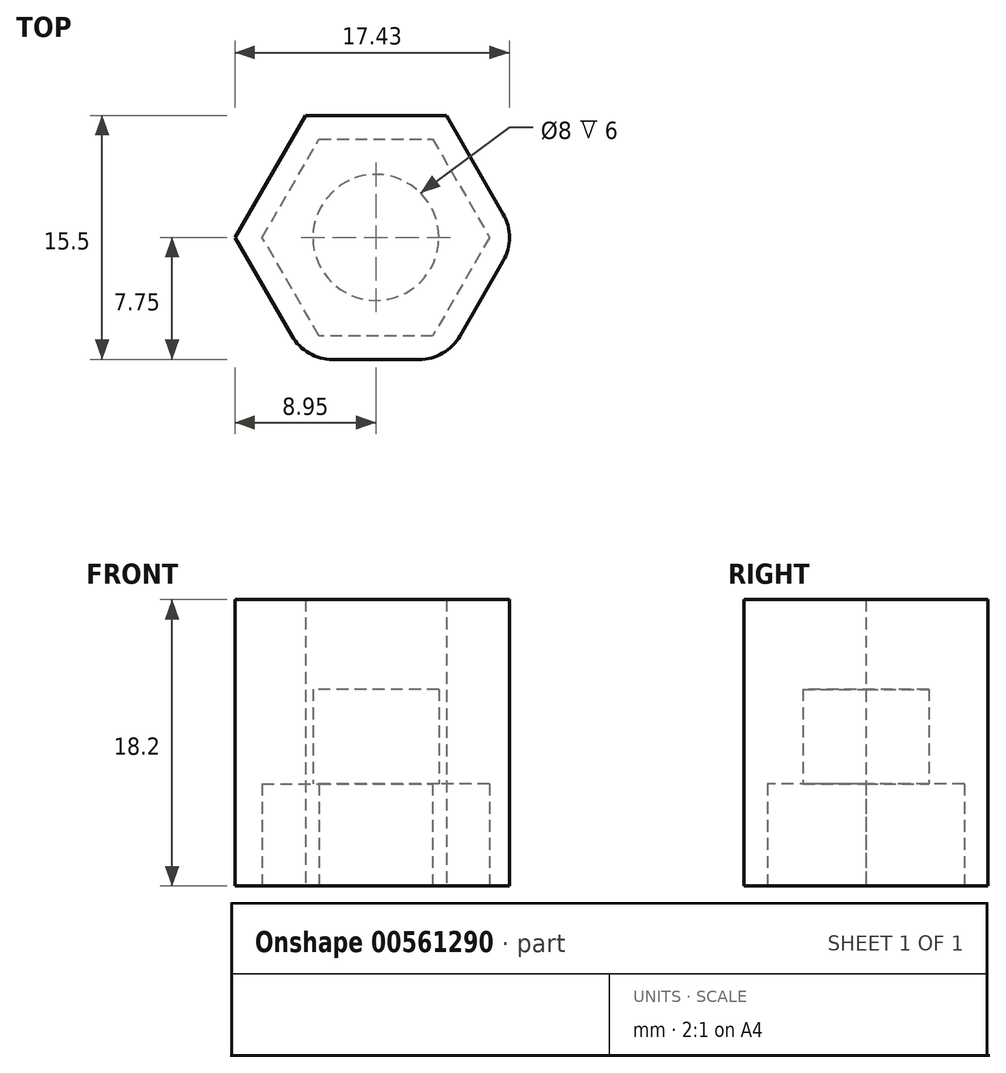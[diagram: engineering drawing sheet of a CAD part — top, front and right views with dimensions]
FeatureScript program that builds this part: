
annotation { "Feature Type Name" : "Feature", "Feature Type Description" : "" }
export const myFeature = defineFeature(function(context is Context, id is Id, definition is map)
    precondition{}
    {
        {
            var Q0;
            Q0=qCreatedBy(makeId("Top.planeOp"),FACE);
            var sketch = newSketch(context, id + "F0", { "sketchPlane" : qUnion([Q0])});
            skCircle(sketch, "E0.cCircle", {"center": v(0, 0) * mm, "radius": 7.75 * mm, "construction": true});
            skLineSegment(sketch, "E0.0", {"start": v(8.95, 0) * mm, "end": v(4.47, -7.75) * mm});
            skLineSegment(sketch, "E0.1", {"start": v(4.47, -7.75) * mm, "end": v(-4.47, -7.75) * mm});
            skLineSegment(sketch, "E0.2", {"start": v(-4.47, -7.75) * mm, "end": v(-8.95, 0) * mm});
            skLineSegment(sketch, "E0.3", {"start": v(-8.95, 0) * mm, "end": v(-4.47, 7.75) * mm});
            skLineSegment(sketch, "E0.4", {"start": v(-4.47, 7.75) * mm, "end": v(4.47, 7.75) * mm});
            skLineSegment(sketch, "E0.5", {"start": v(4.47, 7.75) * mm, "end": v(8.95, 0) * mm});
            skPoint(sketch, "E0.0.midPoint", {"position": v(6.71, -3.88) * mm});
            skSolve(sketch);
        }
        {
            var Q0;
            Q0 = qSketchRegion(id + "F0", true);
            extrude(context, id + "F1", {"entities" : qUnion([Q0]), "depth" : 18.2 * mm, "offsetDistance" : 25 * mm});
        }
        {
            var Q0;
            Q0=qCreatedBy(makeId("Top.planeOp"),FACE);
            var sketch = newSketch(context, id + "F2", { "sketchPlane" : qUnion([Q0])});
            skCircle(sketch, "E1.cCircle", {"center": v(0, 0) * mm, "radius": 6.25 * mm, "construction": true});
            skLineSegment(sketch, "E1.0", {"start": v(7.22, 0) * mm, "end": v(3.6, -6.25) * mm});
            skLineSegment(sketch, "E1.1", {"start": v(3.6, -6.25) * mm, "end": v(-3.6, -6.25) * mm});
            skLineSegment(sketch, "E1.2", {"start": v(-3.6, -6.25) * mm, "end": v(-7.22, 0) * mm});
            skLineSegment(sketch, "E1.3", {"start": v(-7.22, 0) * mm, "end": v(-3.6, 6.25) * mm});
            skLineSegment(sketch, "E1.4", {"start": v(-3.6, 6.25) * mm, "end": v(3.6, 6.25) * mm});
            skLineSegment(sketch, "E1.5", {"start": v(3.6, 6.25) * mm, "end": v(7.22, 0) * mm});
            skPoint(sketch, "E1.0.midPoint", {"position": v(5.41, -3.12) * mm});
            skSolve(sketch);
        }
        {
            var Q0;
            Q0 = qSketchRegion(id + "F2", true);
            extrude(context, id + "F3", {"entities" : qUnion([Q0]), "operationType" : NewBodyOperationType.REMOVE, "depth" : 6.5 * mm, "offsetDistance" : 25 * mm});
        }
        {
            var Q0;
            Q0=qCreatedBy(makeId("Top.planeOp"),FACE);
            var sketch = newSketch(context, id + "F4", { "sketchPlane" : qUnion([Q0])});
            skCircle(sketch, "E2", {"center": v(0, 0) * mm, "radius": 4 * mm});
            skSolve(sketch);
        }
        {
            var Q0;
            Q0 = qSketchRegion(id + "F4", true);
            extrude(context, id + "F5", {"entities" : qUnion([Q0]), "operationType" : NewBodyOperationType.REMOVE, "depth" : 12.5 * mm, "offsetDistance" : 25 * mm});
        }
        {
            var Q0;
            Q0=makeQuery(id+"F1.opExtrude","SWEPT_EDGE",EDGE,{"disambiguationData":[OSD([sQuery(id+"F0.wireOp",EDGE,"E0.0"),sQuery(id+"F0.wireOp",EDGE,"E0.5")])]});
            var Q1;
            Q1=makeQuery(id+"F1.opExtrude","SWEPT_EDGE",EDGE,{"disambiguationData":[OSD([sQuery(id+"F0.wireOp",EDGE,"E0.0"),sQuery(id+"F0.wireOp",EDGE,"E0.1")])]});
            var Q2;
            Q2=makeQuery(id+"F1.opExtrude","SWEPT_EDGE",EDGE,{"disambiguationData":[OSD([sQuery(id+"F0.wireOp",EDGE,"E0.1"),sQuery(id+"F0.wireOp",EDGE,"E0.2")])]});
            fillet(context, id + "F6", {"entities" : qUnion([Q0, Q1, Q2]), "radius" : 3 * mm, "tangentPropagation" : true, "allowEdgeOverflow" : false});
        }
    });
